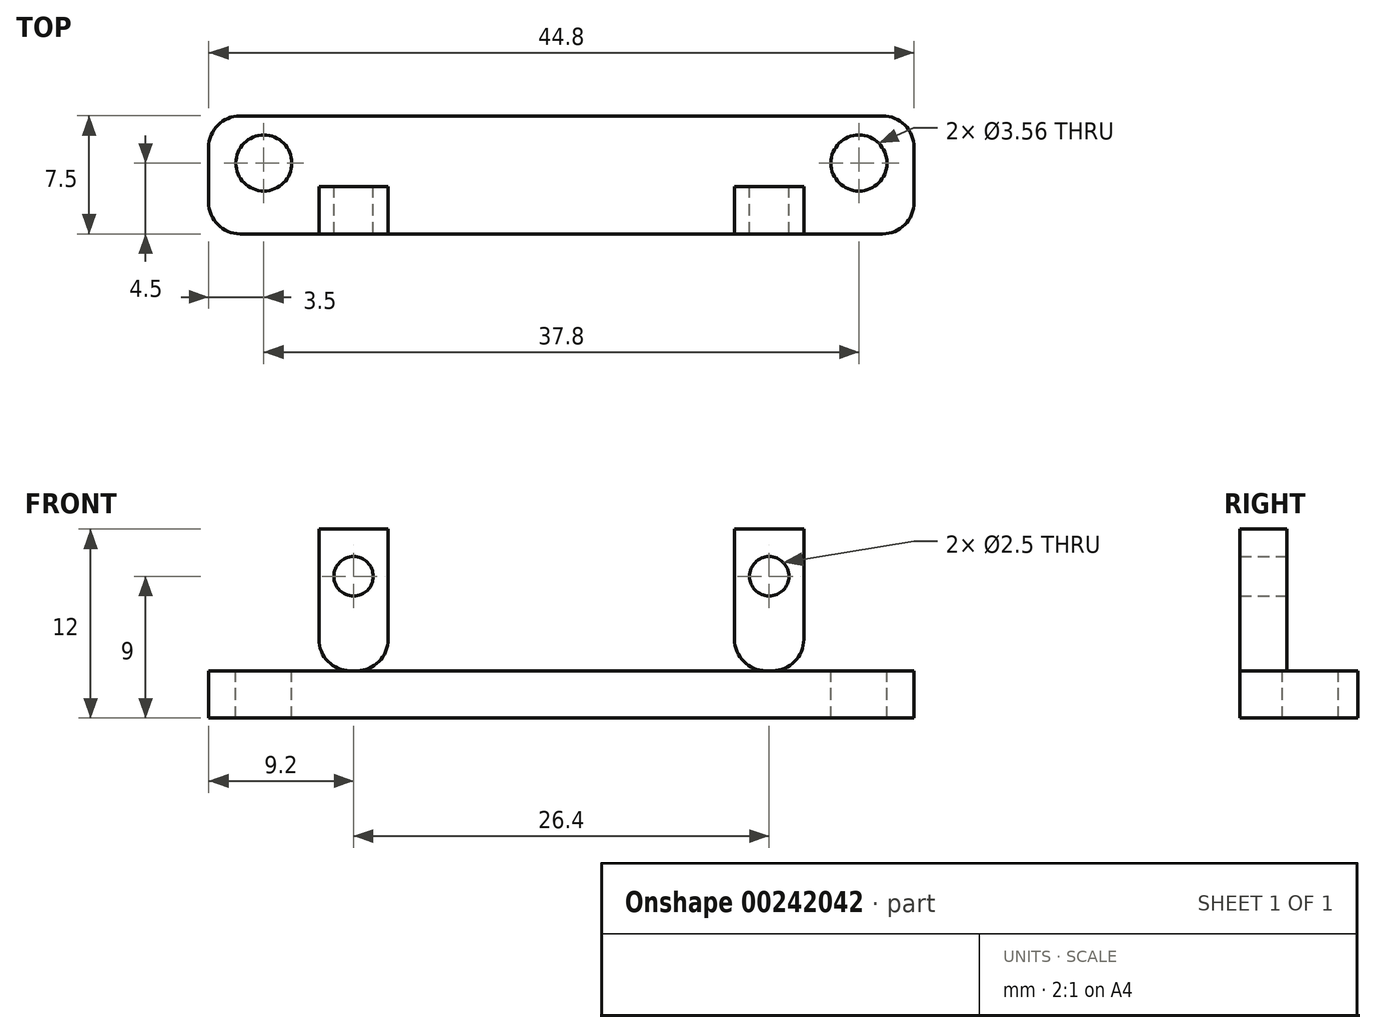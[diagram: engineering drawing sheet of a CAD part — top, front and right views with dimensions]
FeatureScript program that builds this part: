
annotation { "Feature Type Name" : "Feature", "Feature Type Description" : "" }
export const myFeature = defineFeature(function(context is Context, id is Id, definition is map)
    precondition{}
    {
        {
            var Q0;
            Q0=qCreatedBy(makeId("Front.planeOp"),FACE);
            var sketch = newSketch(context, id + "F0", { "sketchPlane" : qUnion([Q0])});
            skLineSegment(sketch, "E0.bottom", {"start": v(0, 0) * mm, "end": v(4.4, 0) * mm});
            skLineSegment(sketch, "E0.top", {"start": v(0, 9) * mm, "end": v(4.4, 9) * mm});
            skLineSegment(sketch, "E0.left", {"start": v(0, 0) * mm, "end": v(0, 9) * mm});
            skLineSegment(sketch, "E0.right", {"start": v(4.4, 0) * mm, "end": v(4.4, 9) * mm});
            skCircle(sketch, "E1", {"center": v(2.2, 6) * mm, "radius": 1.25 * mm});
            skPoint(sketch, "E1.centerSnap0", {"position": v(2.2, 9) * mm});
            skLineSegment(sketch, "E2", {"start": v(15.4, 0) * mm, "end": v(15.4, 9.62) * mm, "construction": true});
            skLineSegment(sketch, "E3.MirrorCS", {"start": v(30.8, 9) * mm, "end": v(26.4, 9) * mm});
            skPoint(sketch, "E4.MirrorP", {"position": v(28.6, 9) * mm});
            skLineSegment(sketch, "E5.MirrorCS", {"start": v(30.8, 0) * mm, "end": v(26.4, 0) * mm});
            skLineSegment(sketch, "E6.MirrorCS", {"start": v(30.8, 0) * mm, "end": v(30.8, 9) * mm});
            skLineSegment(sketch, "E7.MirrorCS", {"start": v(26.4, 0) * mm, "end": v(26.4, 9) * mm});
            skCircle(sketch, "E8.MirrorC", {"center": v(28.6, 6) * mm, "radius": 1.25 * mm});
            skSolve(sketch);
        }
        {
            var Q0;
            Q0 = qSketchRegion(id + "F0", true);
            extrude(context, id + "F1", {"entities" : qUnion([Q0]), "depth" : 3 * mm});
        }
        {
            var Q0;
            Q0=qCreatedBy(makeId("Top.planeOp"),FACE);
            var sketch = newSketch(context, id + "F2", { "sketchPlane" : qUnion([Q0])});
            skLineSegment(sketch, "E9.bottom", {"start": v(-7, -3) * mm, "end": v(37.8, -3) * mm});
            skLineSegment(sketch, "E9.top", {"start": v(-7, 4.5) * mm, "end": v(37.8, 4.5) * mm});
            skLineSegment(sketch, "E9.left", {"start": v(-7, -3) * mm, "end": v(-7, 4.5) * mm});
            skLineSegment(sketch, "E9.right", {"start": v(37.8, -3) * mm, "end": v(37.8, 4.5) * mm});
            skCircle(sketch, "E10", {"center": v(34.3, 1.5) * mm, "radius": 1.78 * mm});
            skLineSegment(sketch, "E11", {"start": v(15.4, 4.5) * mm, "end": v(15.4, -3) * mm, "construction": true});
            skCircle(sketch, "E12.MirrorC", {"center": v(-3.5, 1.5) * mm, "radius": 1.78 * mm});
            skSolve(sketch);
        }
        {
            var Q0;
            Q0 = qSketchRegion(id + "F2", true);
            extrude(context, id + "F3", {"entities" : qUnion([Q0]), "oppositeDirection" : true, "depth" : 3 * mm});
        }
        {
            var Q0;
            Q0=makeQuery(id+"F1.opExtrude","SWEPT_EDGE",EDGE,{"disambiguationData":[OSD([sQuery(id+"F0.wireOp",EDGE,"E0.bottom"),sQuery(id+"F0.wireOp",EDGE,"E0.left")])]});
            var Q1;
            Q1=makeQuery(id+"F1.opExtrude","SWEPT_EDGE",EDGE,{"disambiguationData":[OSD([sQuery(id+"F0.wireOp",EDGE,"E0.bottom"),sQuery(id+"F0.wireOp",EDGE,"E0.right")])]});
            var Q2;
            Q2=makeQuery(id+"F1.opExtrude","SWEPT_EDGE",EDGE,{"disambiguationData":[OSD([sQuery(id+"F0.wireOp",EDGE,"E5.MirrorCS"),sQuery(id+"F0.wireOp",EDGE,"E7.MirrorCS")])]});
            var Q3;
            Q3=makeQuery(id+"F1.opExtrude","SWEPT_EDGE",EDGE,{"disambiguationData":[OSD([sQuery(id+"F0.wireOp",EDGE,"E5.MirrorCS"),sQuery(id+"F0.wireOp",EDGE,"E6.MirrorCS")])]});
            fillet(context, id + "F4", {"entities" : qUnion([Q0, Q1, Q2, Q3]), "radius" : 2 * mm, "tangentPropagation" : true, "allowEdgeOverflow" : false});
        }
        {
            var Q0;
            Q0=makeQuery(id+"F3.opExtrude","SWEPT_EDGE",EDGE,{"disambiguationData":[OSD([sQuery(id+"F2.wireOp",EDGE,"E9.bottom"),sQuery(id+"F2.wireOp",EDGE,"E9.left")])]});
            var Q1;
            Q1=makeQuery(id+"F3.opExtrude","SWEPT_EDGE",EDGE,{"disambiguationData":[OSD([sQuery(id+"F2.wireOp",EDGE,"E9.top"),sQuery(id+"F2.wireOp",EDGE,"E9.left")])]});
            var Q2;
            Q2=makeQuery(id+"F3.opExtrude","SWEPT_EDGE",EDGE,{"disambiguationData":[OSD([sQuery(id+"F2.wireOp",EDGE,"E9.bottom"),sQuery(id+"F2.wireOp",EDGE,"E9.right")])]});
            var Q3;
            Q3=makeQuery(id+"F3.opExtrude","SWEPT_EDGE",EDGE,{"disambiguationData":[OSD([sQuery(id+"F2.wireOp",EDGE,"E9.top"),sQuery(id+"F2.wireOp",EDGE,"E9.right")])]});
            fillet(context, id + "F5", {"entities" : qUnion([Q0, Q1, Q2, Q3]), "radius" : 2 * mm, "tangentPropagation" : true, "allowEdgeOverflow" : false});
        }
    });
